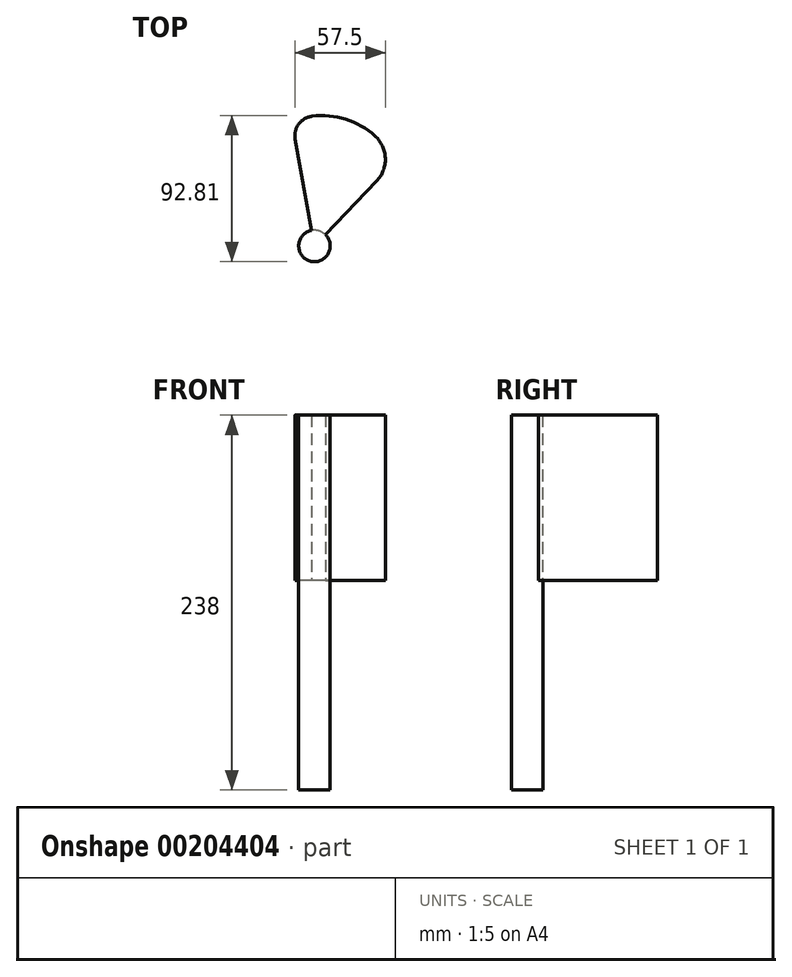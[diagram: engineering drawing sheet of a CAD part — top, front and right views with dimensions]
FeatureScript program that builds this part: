
annotation { "Feature Type Name" : "Feature", "Feature Type Description" : "" }
export const myFeature = defineFeature(function(context is Context, id is Id, definition is map)
    precondition{}
    {
        {
            var Q0;
            Q0=qCreatedBy(makeId("Top.planeOp"),FACE);
            var sketch = newSketch(context, id + "F0", { "sketchPlane" : qUnion([Q0])});
            skArc(sketch, "E0", {"start": v(-1.79, 9.84) * mm, "mid": v(-2.88, -9.58) * mm, "end": v(6.92, 7.22) * mm});
            skArc(sketch, "E1", {"start": v(-1.6, 82.4) * mm, "mid": v(-10.1, 77.38) * mm, "end": v(-12.3, 67.77) * mm});
            skArc(sketch, "E2", {"start": v(38.46, 69.8) * mm, "mid": v(19.82, 80.5) * mm, "end": v(-1.6, 82.4) * mm});
            skArc(sketch, "E3", {"start": v(39.44, 41.16) * mm, "mid": v(44.99, 55.69) * mm, "end": v(38.46, 69.8) * mm});
            skPoint(sketch, "E4", {"position": v(-1.6, 82.4) * mm});
            skPoint(sketch, "E5", {"position": v(38.46, 69.8) * mm});
            skLineSegment(sketch, "E6", {"start": v(6.92, 7.22) * mm, "end": v(39.44, 41.16) * mm});
            skLineSegment(sketch, "E7", {"start": v(-1.79, 9.84) * mm, "end": v(-12.3, 67.77) * mm});
            skSolve(sketch);
        }
        {
            var Q0;
            Q0=makeQuery(id+"F0.imprint","IMPRINT",FACE,{"disambiguationData":[TD([[makeQuery(id+"F0.imprint","IMPRINT",EDGE,{"derivedFrom":sQuery(id+"F0.wireOp",EDGE,"E0")}),1.0]])]});
            extrude(context, id + "F1", {"entities" : qUnion([Q0]), "depth" : 105.1 * mm});
        }
        {
            var Q0;
            Q0=makeQuery(id+"F0.imprint","IMPRINT",FACE,{"disambiguationData":[TD([[makeQuery(id+"F0.imprint","IMPRINT",EDGE,{"derivedFrom":sQuery(id+"F0.wireOp",EDGE,"E0")}),1.0]])]});
            var sketch = newSketch(context, id + "F2", { "sketchPlane" : qUnion([Q0])});
            skCircle(sketch, "E8", {"center": v(0, 0) * mm, "radius": 10 * mm});
            skSolve(sketch);
        }
        {
            var Q0;
            {var subQ0=sQuery(id+"F2.wireOp",EDGE,"E8");var subQ1=makeQuery(id+"F2.imprint","INTERSECT",VERTEX,{"derivedFrom":[makeQuery(id+"F0.imprint","IMPRINT",EDGE,{"derivedFrom":sQuery(id+"F0.wireOp",EDGE,"E7")}),subQ0]});Q0=makeQuery(id+"F2.imprint","IMPRINT",FACE,{"disambiguationData":[TD([[makeQuery(id+"F2.imprint","IMPRINT",EDGE,{"disambiguationData":[TD([[subQ1,-1.0]])],"derivedFrom":subQ0}),1.0]])]});}
            extrude(context, id + "F3", {"entities" : qUnion([Q0]), "operationType" : NewBodyOperationType.ADD, "oppositeDirection" : true, "depth" : 132.9 * mm});
        }
    });
